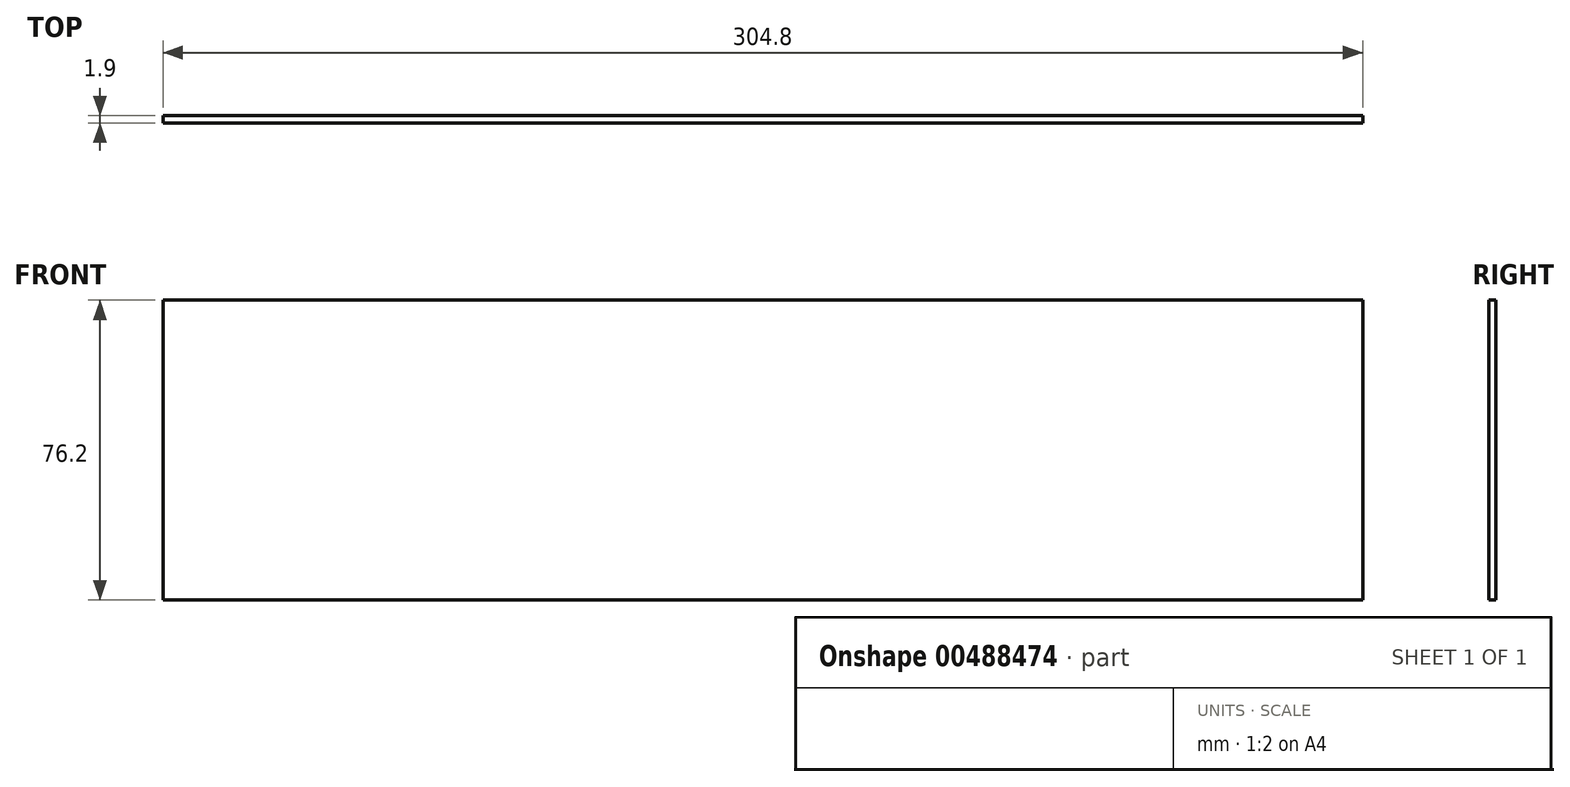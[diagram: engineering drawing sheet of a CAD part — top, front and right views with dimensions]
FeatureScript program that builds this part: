
annotation { "Feature Type Name" : "Feature", "Feature Type Description" : "" }
export const myFeature = defineFeature(function(context is Context, id is Id, definition is map)
    precondition{}
    {
        {
            var Q0;
            Q0=qCreatedBy(makeId("Front.planeOp"),FACE);
            var sketch = newSketch(context, id + "F0", { "sketchPlane" : qUnion([Q0])});
            skLineSegment(sketch, "E0.bottom", {"start": v(152.4, 38.1) * mm, "end": v(-152.4, 38.1) * mm});
            skLineSegment(sketch, "E0.top", {"start": v(152.4, -38.1) * mm, "end": v(-152.4, -38.1) * mm});
            skLineSegment(sketch, "E0.left", {"start": v(152.4, 38.1) * mm, "end": v(152.4, -38.1) * mm});
            skLineSegment(sketch, "E0.right", {"start": v(-152.4, 38.1) * mm, "end": v(-152.4, -38.1) * mm});
            skPoint(sketch, "E0.middle", {"position": v(0, 0) * mm});
            skSolve(sketch);
        }
        {
            var Q0;
            Q0 = qSketchRegion(id + "F0", true);
            extrude(context, id + "F1", {"entities" : qUnion([Q0]), "depth" : 1.9 * mm});
        }
    });
